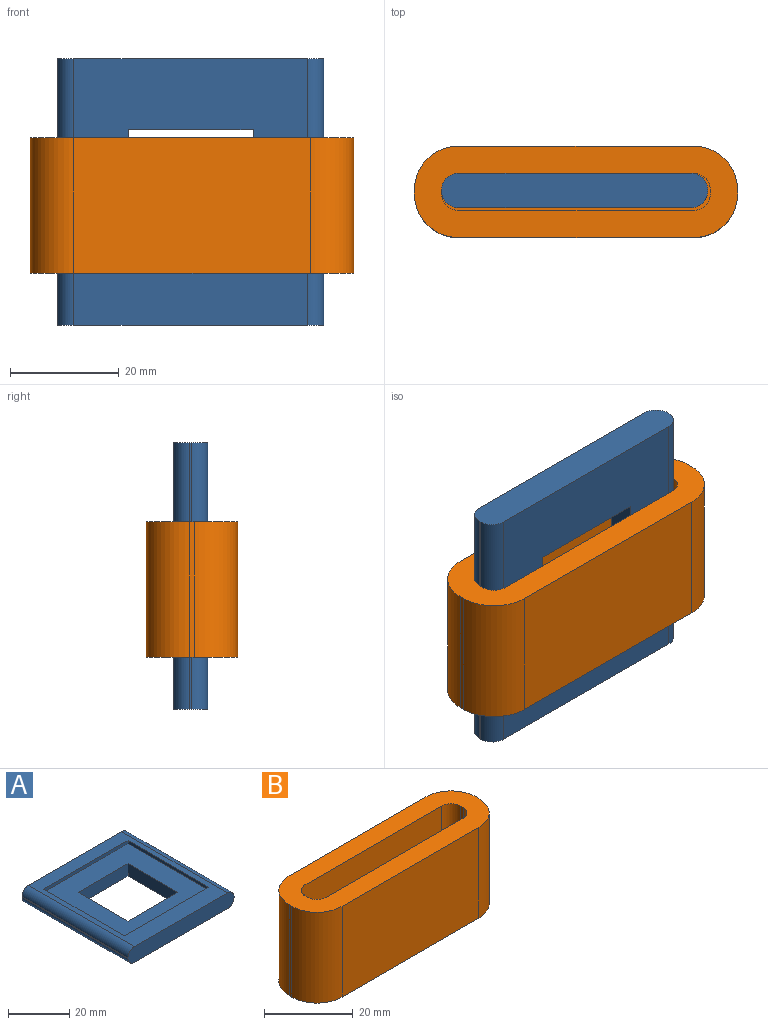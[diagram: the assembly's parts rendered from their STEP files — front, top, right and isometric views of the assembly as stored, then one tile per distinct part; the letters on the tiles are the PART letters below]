
ASSEMBLY  parts=2 mates=1
PART A: 19 faces, bbox 49x49x6.3 mm
  f0: plane 49x6.3mm, normal (0,-1,0), area 301mm2, adj f1,f6,f7,f8,f15,f16,f17,f18
  f1: plane 49x0.3mm, normal (1,0,0), area 14.7mm2, adj f0,f2,f15,f17
  f2: plane 49x6.3mm, normal (0,1,0), area 301mm2, adj f1,f6,f7,f8,f15,f16,f17,f18
  f3: plane 39x1.3mm, normal (-1,0,0), area 49.7mm2, adj f5,f7,f13,f14
  f4: plane 39x1.3mm, normal (1,0,0), area 49.7mm2, adj f5,f7,f13,f14
  f5: plane 39x1.3mm, normal (0,-1,0), area 50.7mm2, adj f3,f4,f7,f13
  f6: plane 49x0.3mm, normal (-1,0,0), area 14.7mm2, adj f0,f2,f16,f18
  f7: plane 49x43mm, normal (0,0,1), area 647.1mm2, adj f0,f2,f3,f4,f5,f14,f17,f18
  f8: plane 49x43mm, normal (0,0,-1), area 1578mm2, adj f0,f2,f9,f10,f11,f12,f15,f16
  f9: plane 23x5mm, normal (-1,0,0), area 115mm2, adj f8,f10,f12,f13
  f10: plane 23x5mm, normal (0,1,0), area 115mm2, adj f8,f9,f11,f13
  f11: plane 23x5mm, normal (1,0,0), area 115mm2, adj f8,f10,f12,f13
  f12: plane 23x5mm, normal (0,-1,0), area 115mm2, adj f8,f9,f11,f13
  f13: plane 39x39mm, normal (0,0,1), area 992mm2, adj f3,f4,f5,f9,f10,f11,f12,f14
  f14: plane 39x1.57mm, normal (0,0.64,-0.77), area 79.4mm2, adj f3,f4,f7,f13
  f15: cylinder r=3mm len=49mm, axis (0,1,0), area 230.9mm2, adj f0,f1,f2,f8
  f16: cylinder r=3mm len=49mm, axis (0,-1,0), area 230.9mm2, adj f0,f2,f6,f8
  f17: cylinder r=3mm len=49mm, axis (0,-1,0), area 230.9mm2, adj f0,f1,f2,f7
  f18: cylinder r=3mm len=49mm, axis (0,1,0), area 230.9mm2, adj f0,f2,f6,f7
PART B: 19 faces, bbox 59.5x16.8x25 mm
  f0: plane 59.5x16.8mm, normal (0,0,-1), area 944.7mm2, adj f5,f6,f7,f8,f11,f12,f13,f14
  f1: plane 43.5x20mm, normal (0,1,0), area 870mm2, adj f9,f10,f15,f16
  f2: plane 20x0.8mm, normal (-1,0,0), area 16mm2, adj f9,f10,f15,f18
  f3: plane 43.5x20mm, normal (0,-1,0), area 870mm2, adj f9,f10,f17,f18
  f4: plane 20x0.8mm, normal (1,0,0), area 16mm2, adj f9,f10,f16,f17
  f5: plane 43.5x25mm, normal (0,-1,0), area 1087.5mm2, adj f0,f9,f11,f14
  f6: plane 25x0.8mm, normal (1,0,0), area 20mm2, adj f0,f9,f11,f12
  f7: plane 43.5x25mm, normal (0,1,0), area 1087.5mm2, adj f0,f9,f12,f13
  f8: plane 25x0.8mm, normal (-1,0,0), area 20mm2, adj f0,f9,f13,f14
  f9: plane 59.5x16.8mm, normal (0,0,1), area 615.8mm2, adj f1,f2,f3,f4,f5,f6,f7,f8
  f10: plane 49.5x6.8mm, normal (0,0,1), area 328.9mm2, adj f1,f2,f3,f4,f15,f16,f17,f18
  f11: cylinder r=8mm len=25mm, axis (0,0,1), area 314.2mm2, adj f0,f5,f6,f9
  f12: cylinder r=8mm len=25mm, axis (0,0,-1), area 314.2mm2, adj f0,f6,f7,f9
  f13: cylinder r=8mm len=25mm, axis (0,0,1), area 314.2mm2, adj f0,f7,f8,f9
  f14: cylinder r=8mm len=25mm, axis (0,0,-1), area 314.2mm2, adj f0,f5,f8,f9
  f15: cylinder r=3mm len=20mm, axis (0,0,-1), area 94.2mm2, adj f1,f2,f9,f10
  f16: cylinder r=3mm len=20mm, axis (0,0,1), area 94.2mm2, adj f1,f4,f9,f10
  f17: cylinder r=3mm len=20mm, axis (0,0,-1), area 94.2mm2, adj f3,f4,f9,f10
  f18: cylinder r=3mm len=20mm, axis (0,0,1), area 94.2mm2, adj f2,f3,f9,f10
PLACE A rot(axis=(0,0.71,0.71),180deg) t=(-41.54,-10.32,18.71)mm
PLACE B t=(-41.29,30.34,3.71)mm
MATE slider A.f17 <-> B.f13  axis (0,0,-1) through (-63.04,-7.02,18.71)mm
